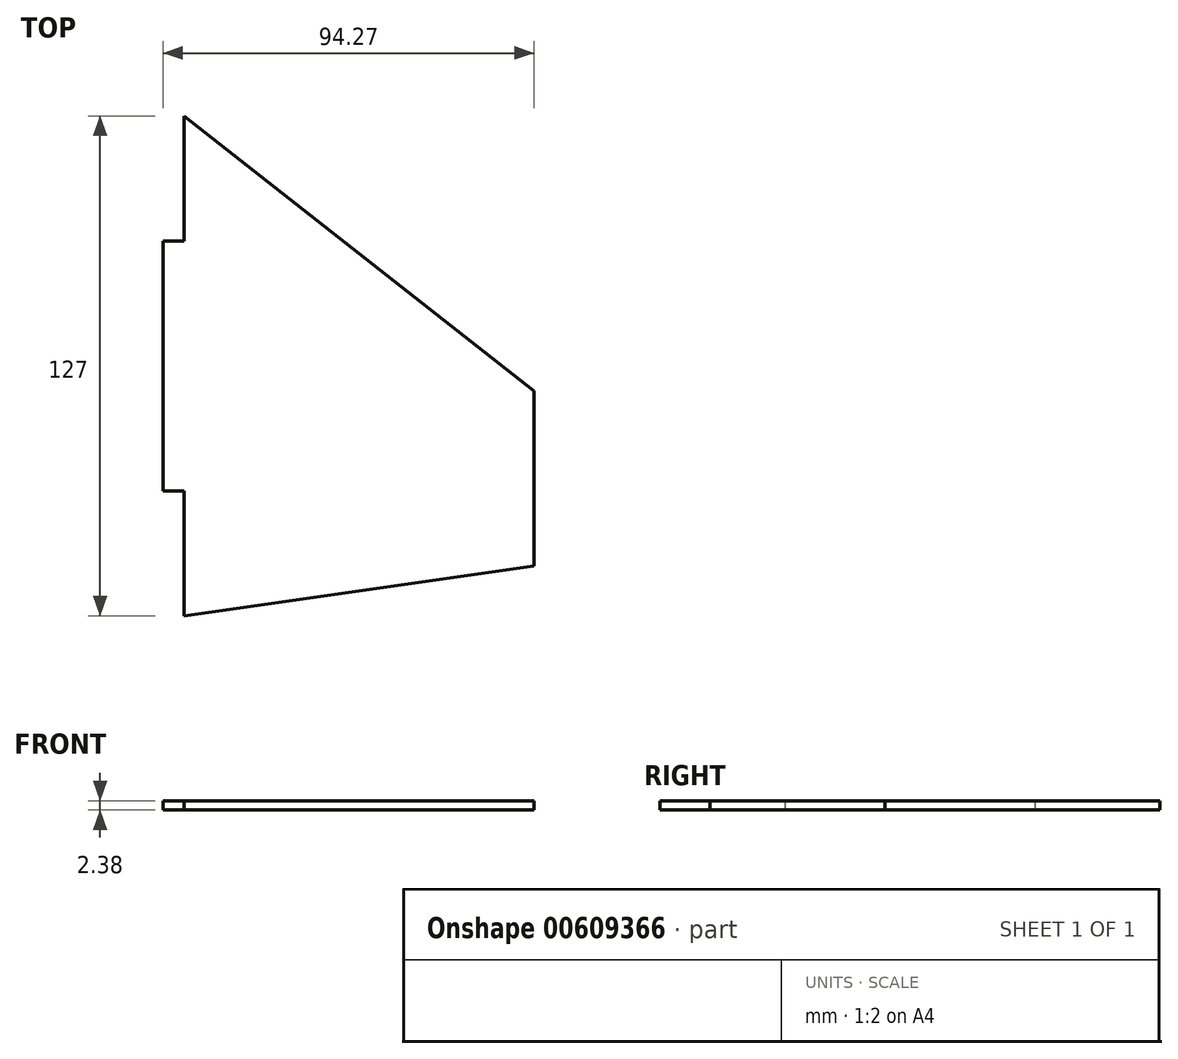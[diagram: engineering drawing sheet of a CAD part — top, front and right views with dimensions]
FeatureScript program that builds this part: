
annotation { "Feature Type Name" : "Feature", "Feature Type Description" : "" }
export const myFeature = defineFeature(function(context is Context, id is Id, definition is map)
    precondition{}
    {
        {
            var Q0;
            Q0=qCreatedBy(makeId("Top.planeOp"),FACE);
            var sketch = newSketch(context, id + "F0", { "sketchPlane" : qUnion([Q0])});
            skLineSegment(sketch, "E0", {"start": v(0, 63.5) * mm, "end": v(0, -63.5) * mm});
            skLineSegment(sketch, "E1", {"start": v(0, -63.5) * mm, "end": v(88.9, -50.8) * mm});
            skLineSegment(sketch, "E2", {"start": v(88.9, -50.8) * mm, "end": v(88.9, -6.35) * mm});
            skLineSegment(sketch, "E3", {"start": v(88.9, -6.35) * mm, "end": v(0, 63.5) * mm});
            skLineSegment(sketch, "E4.bottom", {"start": v(0, -31.75) * mm, "end": v(-5.37, -31.75) * mm});
            skLineSegment(sketch, "E4.top", {"start": v(0, 31.75) * mm, "end": v(-5.37, 31.75) * mm});
            skLineSegment(sketch, "E4.left", {"start": v(0, -31.75) * mm, "end": v(0, 31.75) * mm});
            skLineSegment(sketch, "E4.right", {"start": v(-5.37, -31.75) * mm, "end": v(-5.37, 31.75) * mm});
            skSolve(sketch);
        }
        {
            var Q0;
            {var subQ0=sQuery(id+"F0.wireOp",EDGE,"E1");Q0=makeQuery(id+"F0.imprint","IMPRINT",FACE,{"disambiguationData":[TD([[makeQuery(id+"F0.imprint","IMPRINT",EDGE,{"derivedFrom":subQ0}),1.0]])]});}
            var Q1;
            Q1=makeQuery(id+"F0.imprint","IMPRINT",FACE,{"disambiguationData":[TD([[makeQuery(id+"F0.imprint","IMPRINT",EDGE,{"derivedFrom":sQuery(id+"F0.wireOp",EDGE,"E4.bottom")}),-1.0]])]});
            extrude(context, id + "F1", {"entities" : qUnion([Q0, Q1]), "depth" : 2.38 * mm, "offsetDistance" : 25.4 * mm});
        }
    });
